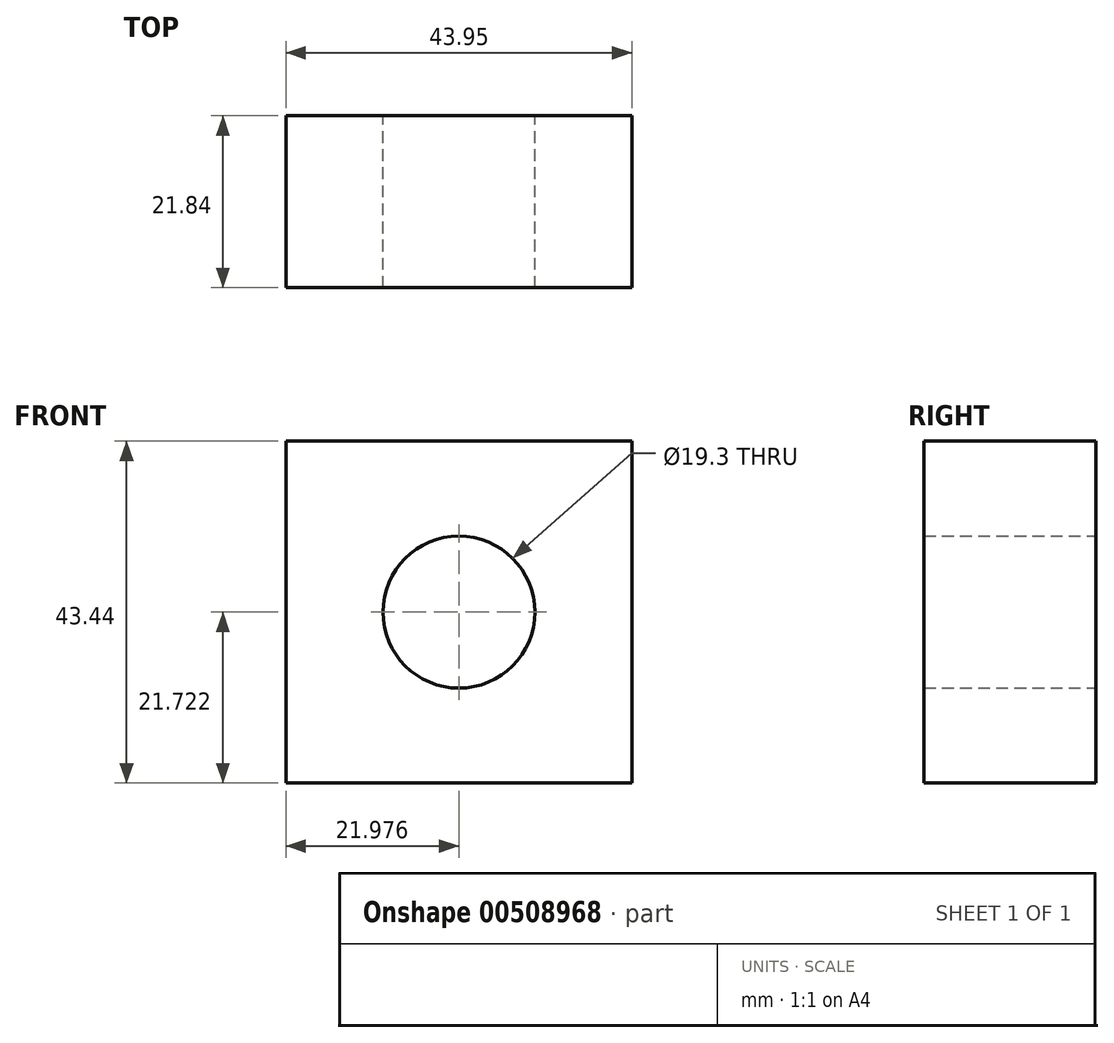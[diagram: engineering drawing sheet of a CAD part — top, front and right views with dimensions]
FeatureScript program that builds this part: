
annotation { "Feature Type Name" : "Feature", "Feature Type Description" : "" }
export const myFeature = defineFeature(function(context is Context, id is Id, definition is map)
    precondition{}
    {
        {
            var Q0;
            Q0=qCreatedBy(makeId("Front.planeOp"),FACE);
            var sketch = newSketch(context, id + "F0", { "sketchPlane" : qUnion([Q0])});
            skLineSegment(sketch, "E0.bottom", {"start": v(-48.2, 51.03) * mm, "end": v(-4.26, 51.03) * mm});
            skLineSegment(sketch, "E0.top", {"start": v(-48.2, 7.6) * mm, "end": v(-4.26, 7.6) * mm});
            skLineSegment(sketch, "E0.left", {"start": v(-48.2, 51.03) * mm, "end": v(-48.2, 7.6) * mm});
            skLineSegment(sketch, "E0.right", {"start": v(-4.26, 51.03) * mm, "end": v(-4.26, 7.6) * mm});
            skLineSegment(sketch, "E1", {"start": v(-26.23, 51.03) * mm, "end": v(-26.23, 7.6) * mm, "construction": true});
            skLineSegment(sketch, "E2", {"start": v(-48.2, 29.31) * mm, "end": v(-4.26, 29.31) * mm, "construction": true});
            skCircle(sketch, "E3", {"center": v(-26.23, 29.31) * mm, "radius": 9.65 * mm});
            skSolve(sketch);
        }
        {
            var Q0;
            Q0=qSketchRegion(id+"F0",true);
            extrude(context, id + "F1", {"entities" : qUnion([Q0]), "depth" : 21.84 * mm});
        }
    });
